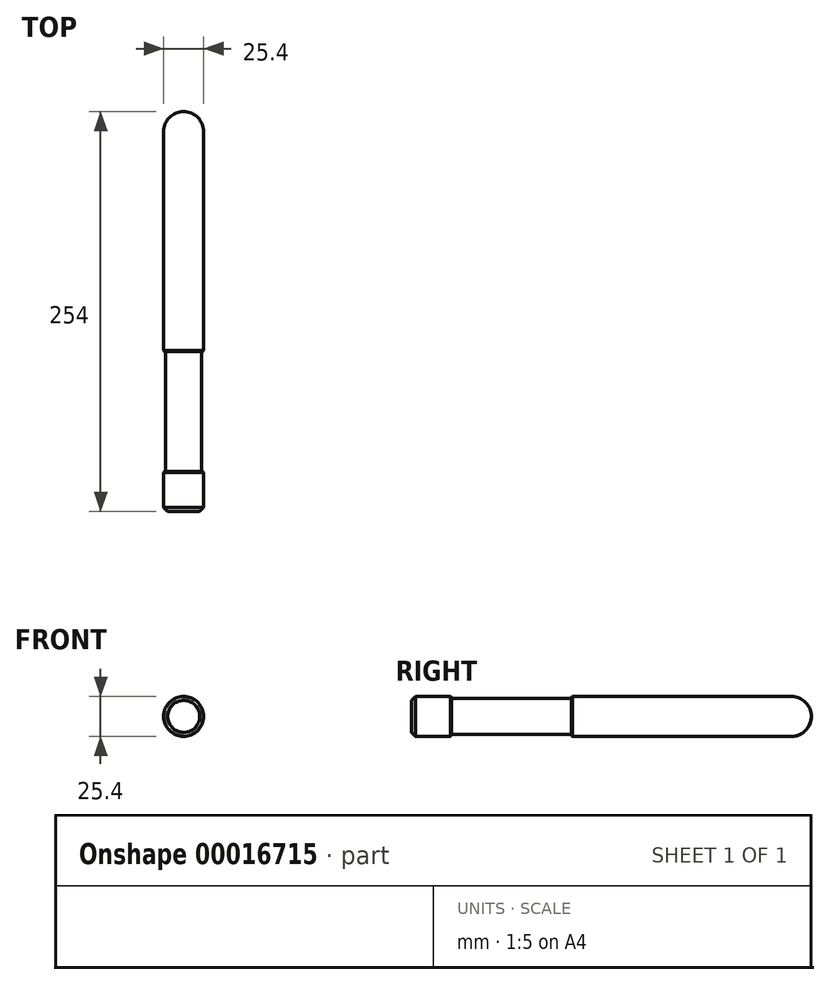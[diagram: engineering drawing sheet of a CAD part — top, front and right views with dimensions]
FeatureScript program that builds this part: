
annotation { "Feature Type Name" : "Feature", "Feature Type Description" : "" }
export const myFeature = defineFeature(function(context is Context, id is Id, definition is map)
    precondition{}
    {
        {
            var Q0;
            Q0=qCreatedBy(makeId("Front.planeOp"),FACE);
            var sketch = newSketch(context, id + "F0", { "sketchPlane" : qUnion([Q0])});
            skCircle(sketch, "E0", {"center": v(0, 0) * mm, "radius": 12.7 * mm});
            skSolve(sketch);
        }
        {
            var Q0;
            Q0 = qSketchRegion(id + "F0", true);
            extrude(context, id + "F1", {"entities" : qUnion([Q0]), "depth" : 254 * mm});
        }
        {
            var Q0;
            Q0=qCreatedBy(makeId("Top.planeOp"),FACE);
            var sketch = newSketch(context, id + "F2", { "sketchPlane" : qUnion([Q0])});
            skCircle(sketch, "E1", {"center": v(0, 20.48) * mm, "radius": 37.43 * mm});
            skSolve(sketch);
        }
        {
            var Q0;
            Q0=qCreatedBy(makeId("Right.planeOp"),FACE);
            var sketch = newSketch(context, id + "F3", { "sketchPlane" : qUnion([Q0])});
            skCircle(sketch, "E2", {"center": v(-12.7, 0) * mm, "radius": 12.7 * mm});
            skSolve(sketch);
        }
        {
            var Q0;
            Q0=makeQuery(id+"F1.opExtrude","CAP_EDGE",EDGE,{"disambiguationData":[OSD([sQuery(id+"F0.wireOp",EDGE,"E0")])],"isStart":true});
            fillet(context, id + "F4", {"entities" : qUnion([Q0]), "radius" : 12.7 * mm, "tangentPropagation" : true, "allowEdgeOverflow" : false});
        }
        {
            var Q0;
            Q0=makeQuery(id+"F1.opExtrude","CAP_EDGE",EDGE,{"disambiguationData":[OSD([sQuery(id+"F0.wireOp",EDGE,"E0")])],"isStart":false});
            chamfer(context, id + "F5", {"entities" : qUnion([Q0]), "width" : 2.54 * mm, "tangentPropagation" : true});
        }
        {
            var Q0;
            Q0=qCreatedBy(makeId("Front.planeOp"),FACE);
            cPlane(context, id + "F6", {"entities" : qUnion([Q0]), "cplaneType" : CPlaneType.OFFSET, "offset" : 228.6 * mm, "width" : 152.4 * mm, "height" : 152.4 * mm});
        }
        {
            var Q0;
            Q0=qCreatedBy(id+"F6.planeOp",FACE);
            var sketch = newSketch(context, id + "F7", { "sketchPlane" : qUnion([Q0])});
            skCircle(sketch, "E3", {"center": v(0, 0) * mm, "radius": 13.97 * mm});
            skCircle(sketch, "E4", {"center": v(0, 0) * mm, "radius": 11.43 * mm});
            skSolve(sketch);
        }
        {
            var Q0;
            Q0 = qSketchRegion(id + "F7", true);
            extrude(context, id + "F8", {"entities" : qUnion([Q0]), "operationType" : NewBodyOperationType.REMOVE, "oppositeDirection" : true, "depth" : 76.2 * mm});
        }
        {
            var Q0;
            Q0=makeQuery(id+"F8.boolean.opBoolean","COPY",EDGE,{"derivedFrom":makeQuery(id+"F8.opExtrude","CAP_EDGE",EDGE,{"disambiguationData":[OSD([sQuery(id+"F7.wireOp",EDGE,"E4")])],"isStart":false})});
            var Q1;
            Q1=makeQuery(id+"F8.boolean.opBoolean","COPY",EDGE,{"derivedFrom":makeQuery(id+"F8.opExtrude","CAP_EDGE",EDGE,{"disambiguationData":[OSD([sQuery(id+"F7.wireOp",EDGE,"E4")])],"isStart":true})});
            fillet(context, id + "F9", {"entities" : qUnion([Q0, Q1]), "radius" : 0.64 * mm, "tangentPropagation" : true, "allowEdgeOverflow" : false});
        }
        {
            var Q0;
            Q0=makeQuery(id+"F8.boolean.opBoolean","INTERSECT",EDGE,{"derivedFrom":[makeQuery(id+"F1.opExtrude","SWEPT_FACE",FACE,{"disambiguationData":[OSD([sQuery(id+"F0.wireOp",EDGE,"E0")])]}),makeQuery(id+"F8.opExtrude","CAP_FACE",FACE,{"disambiguationData":[OSD([sQuery(id+"F7.wireOp",EDGE,"E3"),sQuery(id+"F7.wireOp",EDGE,"E4")])],"isStart":false})]});
            var Q1;
            Q1=makeQuery(id+"F8.boolean.opBoolean","INTERSECT",EDGE,{"derivedFrom":[makeQuery(id+"F1.opExtrude","SWEPT_FACE",FACE,{"disambiguationData":[OSD([sQuery(id+"F0.wireOp",EDGE,"E0")])]}),makeQuery(id+"F8.opExtrude","CAP_FACE",FACE,{"disambiguationData":[OSD([sQuery(id+"F7.wireOp",EDGE,"E3"),sQuery(id+"F7.wireOp",EDGE,"E4")])],"isStart":true})]});
            chamfer(context, id + "F10", {"entities" : qUnion([Q0, Q1]), "width" : 0.64 * mm, "tangentPropagation" : true});
        }
    });
